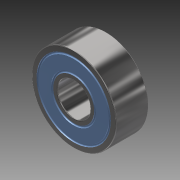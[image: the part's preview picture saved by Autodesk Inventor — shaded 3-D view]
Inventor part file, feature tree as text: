
AUTODESK INVENTOR PART (.ipt)
format: ipt  version: 2014 (Build 180170000, 170)  size: 184,832 bytes
history: native  units: in
note: dims shown in document units (in); Inventor stores cm internally (conversion verified against a paired STEP export)
features: sketch x2, extrude x1, fillet x1, revolve x1, plane x1, mirror x1
ambient origin geometry x8: Origin, YZ Plane, XZ Plane, XY Plane, X Axis, Y Axis, Z Axis, Center Point
bodies: Solid1 (feature_tree)
feature tree (7):
  extrude  "Extrusion1"  Depth=0.3937in
  fillet  "Fillet1"  Radius=0.3937in
  revolve  "Revolution1"  Angle=90.0deg
  plane  "Work Plane1"
  mirror  "Mirror1"
  sketch  "Sketch1"  dims[d0=0.3937in d1=1.0236in d2=0.3937in d3=0.0in]
  sketch  "Sketch2"  dims[d4=0.0118in d5=90.0deg]
